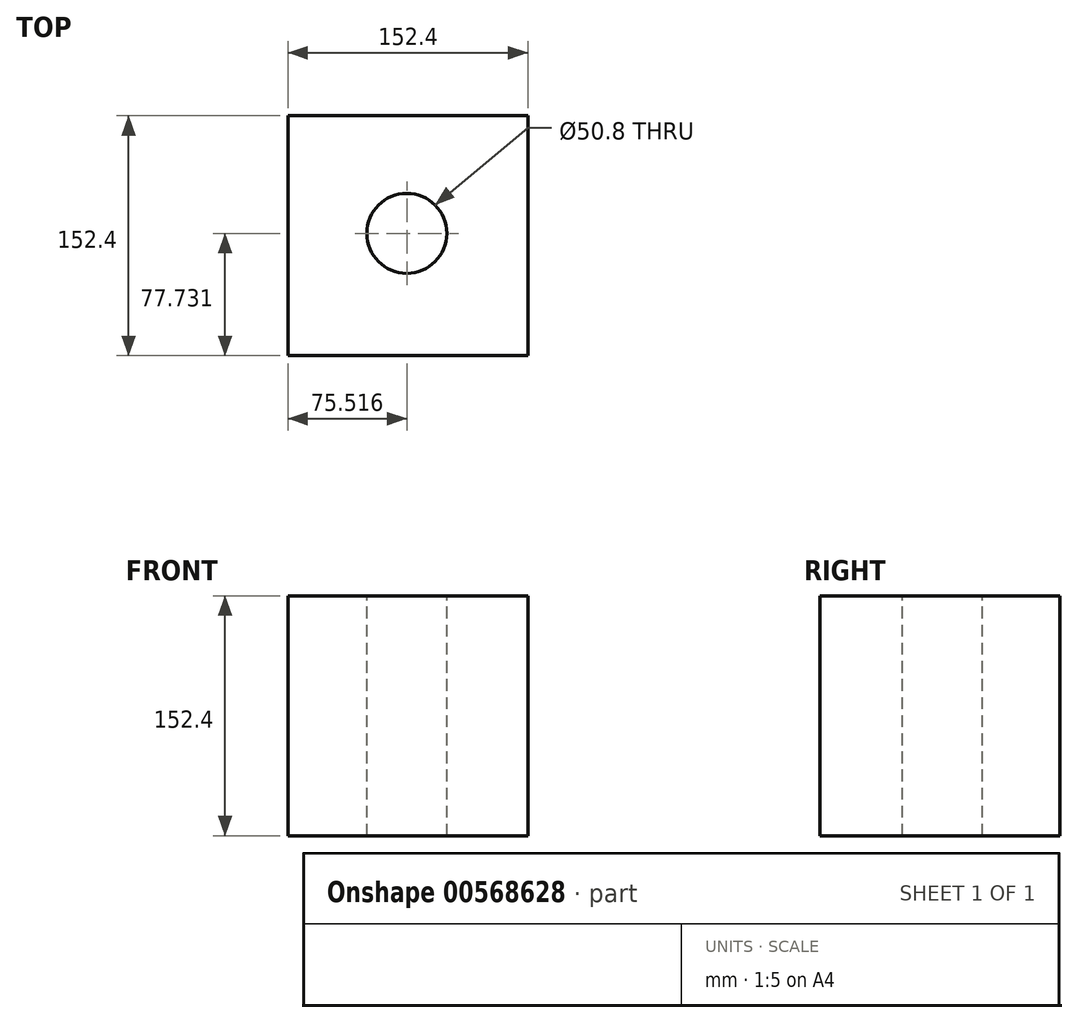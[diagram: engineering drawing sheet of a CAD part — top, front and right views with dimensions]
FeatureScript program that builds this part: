
annotation { "Feature Type Name" : "Feature", "Feature Type Description" : "" }
export const myFeature = defineFeature(function(context is Context, id is Id, definition is map)
    precondition{}
    {
        {
            var Q0;
            Q0=qCreatedBy(makeId("Right.planeOp"),FACE);
            var sketch = newSketch(context, id + "F0", { "sketchPlane" : qUnion([Q0])});
            skLineSegment(sketch, "E0.bottom", {"start": v(0, 0) * mm, "end": v(152.4, 0) * mm});
            skLineSegment(sketch, "E0.top", {"start": v(0, -152.4) * mm, "end": v(152.4, -152.4) * mm});
            skLineSegment(sketch, "E0.left", {"start": v(0, 0) * mm, "end": v(0, -152.4) * mm});
            skLineSegment(sketch, "E0.right", {"start": v(152.4, 0) * mm, "end": v(152.4, -152.4) * mm});
            skSolve(sketch);
        }
        {
            var Q0;
            Q0=makeQuery(id+"F0.imprint","IMPRINT",FACE,{"disambiguationData":[TD([[makeQuery(id+"F0.imprint","IMPRINT",EDGE,{"derivedFrom":sQuery(id+"F0.wireOp",EDGE,"E0.bottom")}),-1.0]])]});
            extrude(context, id + "F1", {"entities" : qUnion([Q0]), "depth" : 152.4 * mm, "offsetDistance" : 25.4 * mm});
        }
        {
            var Q0;
            Q0=makeQuery(id+"F1.opExtrude","SWEPT_FACE",FACE,{"disambiguationData":[OSD([sQuery(id+"F0.wireOp",EDGE,"E0.bottom")])]});
            var sketch = newSketch(context, id + "F2", { "sketchPlane" : qUnion([Q0])});
            skCircle(sketch, "E1", {"center": v(75.52, 77.73) * mm, "radius": 25.4 * mm});
            skSolve(sketch);
        }
        {
            var Q0;
            Q0=makeQuery(id+"F2.imprint","IMPRINT",FACE,{"disambiguationData":[TD([[makeQuery(id+"F2.imprint","IMPRINT",EDGE,{"derivedFrom":sQuery(id+"F2.wireOp",EDGE,"E1")}),1.0]])]});
            extrude(context, id + "F3", {"entities" : qUnion([Q0]), "operationType" : NewBodyOperationType.REMOVE, "endBound" : BoundingType.THROUGH_ALL, "oppositeDirection" : true, "depth" : 50.8 * mm, "offsetDistance" : 25.4 * mm});
        }
    });
